# Revit family: xxxShower_System-American_Standard-Spectra_Versa-9038804_Series
name_source: partatom
category: Plumbing Fixtures
units: mm (PartAtom-declared; Revit-internal decimal feet)

## family parameters
Cut with Voids When Loaded = No
Host = Face
OmniClass Number = 23.45.05.14.17
OmniClass Title = Showers
Part Type = Normal
Room Calculation Point = No
Round Connector Dimension = Use Diameter
Shared = Yes

## types (3) — shared parameters
3-Function Push-Button Diverter = Yes
69" Hose = Yes
ASME A112.18.1/CSA B125.1 = Yes
Assembly Code = D2020300
Bar Height = 24"
CEC Compliant = Yes
CSA B125.1 = Yes
CW Connection = Yes
CWFU = 3
CalGreen Compliant = Yes
Cold Water Connection Diameter = 1/2"
Default Elevation = 44"
Description = Spectra Versa® 24-Inch 4-Function 1.8 gpm/6.8 L/min Shower System With Rain Showerhead
EPA WaterSense = Yes
Flow Rate = 1.8 gpm/6.8 L/min
Grab Bar (1"- 2 5/16") = 1"
Grab Bar Distance = 1"
HW Connection = Yes
HWFU = 3
Height = 32 1/8"
Hot Water Connection Diameter = 1/2"
Installation Instruction Link = https://americanstandard.box.com
Installation Type = Wall Mounted
Length = 6 1/4"
Manufacturer = American Standard
Price = Prices may vary. Please consult Manufacturer Representative for most up-to-date price list.
Product Documentation Link = https://americanstandard.box.com
Product Page URL = https://www.americanstandard-us.com
Revised Date = 03/18/2022
Slide Bar with Easy Glide Holder = Yes
Spectra+™ 11" Rain shower head = Yes
Spectra+™ 4 Function Hand Shower = Yes
Tempered Water Connection = Yes
Tempered Water Connection Diameter = 1/2"
URL = https://www.americanstandard-us.com
Vent Connection = No
WFU = 4
Waste Connection = No
Width = 5 7/16"
cUPC Compliant = Yes

## per-type parameters (varying)
| type | Finish | Material | Showerhead |
| 9038804.002 | Metal-American Standard-002-Polished Chrome | Metal-American Standard-002-Polished Chrome | Showerhead-American_Standard-Spectra_Rain-9038001_Series : 9038001.002 |
| 9038804.278 | Metal-American Standard-278-Legacy Bronze | Metal-American Standard-278-Legacy Bronze | Showerhead-American_Standard-Spectra_Rain-9038001_Series : 9038001.278 |
| 9038804.295 | Metal-American Standard-295-Brushed Nickel | Metal-American Standard-295-Brushed Nickel | Showerhead-American_Standard-Spectra_Rain-9038001_Series : 9038001.295 |

note: column(s) folded — value = type name in every type: Model

## geometry (parser evidence)
native form markers: Sweep x2
no freeform markers — native parametric forms only
